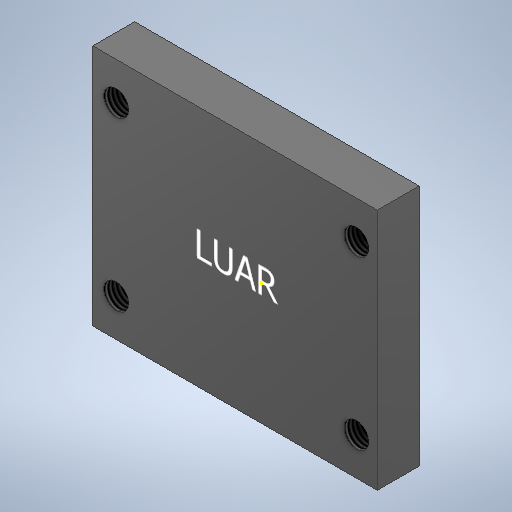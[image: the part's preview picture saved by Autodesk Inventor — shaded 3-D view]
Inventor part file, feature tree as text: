
AUTODESK INVENTOR PART (.ipt)
format: ipt  version: 2025.1 (Build 291241000, 241)  size: 251,904 bytes
history: native  units: in
note: dims shown in document units (in); Inventor stores cm internally (conversion verified against a paired STEP export)
features: thread x4, sketch x2, extrude x1
ambient origin geometry x8: Origin, YZ Plane, XZ Plane, XY Plane, X Axis, Y Axis, Z Axis, Center Point
bodies: Solid1 (feature_tree)
feature tree (7):
  extrude  "Extrusion1"  Depth=1.3386in
  thread  "Thread1"  [1 undecoded]
  thread  "Thread2"  [1 undecoded]
  thread  "Thread3"  [1 undecoded]
  thread  "Thread4"  [1 undecoded]
  sketch  "Sketch3"  dims[d10=0.7874in d11=1.1417in d12=0.1772in d13=0.1969in d14=0.0in d15=0.1969in d16=0.0in d17=0.1969in d18=0.0in d19=0.1969in d20=0.0in d21=0.1969in d22=0.0in]
  sketch  "Sketch1"  dims[d1=1.3386in d2=0.1181in d3=0.1181in d4=0.7874in d5=0.1181in d6=0.1181in d8=1.1299in d9=0.0984in]
note: 4 required parameter values undecoded (feature->parameter linkage not recoverable at this tier; creation-order binding heuristic only, values carry confidence <= 0.55)
